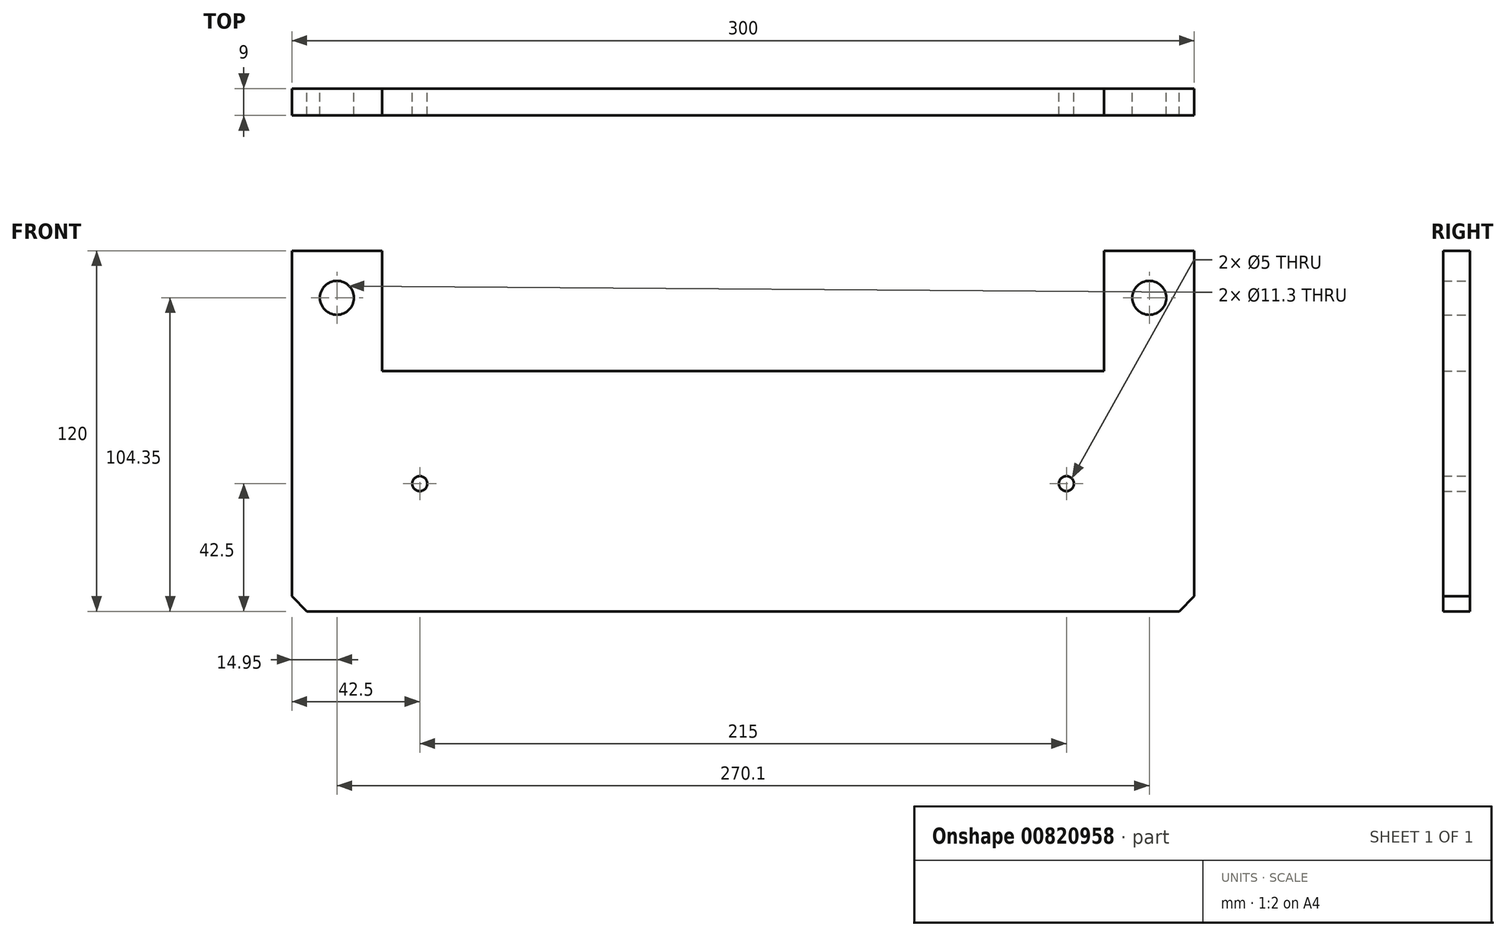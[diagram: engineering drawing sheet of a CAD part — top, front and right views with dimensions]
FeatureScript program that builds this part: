
annotation { "Feature Type Name" : "Feature", "Feature Type Description" : "" }
export const myFeature = defineFeature(function(context is Context, id is Id, definition is map)
    precondition{}
    {
        {
            var Q0;
            Q0=qCreatedBy(makeId("Front.planeOp"),FACE);
            var sketch = newSketch(context, id + "F0", { "sketchPlane" : qUnion([Q0])});
            skCircle(sketch, "E0", {"center": v(-107.5, 42.5) * mm, "radius": 2.5 * mm});
            skLineSegment(sketch, "E1", {"start": v(-150, 120) * mm, "end": v(-120, 120) * mm});
            skLineSegment(sketch, "E2", {"start": v(-120, 120) * mm, "end": v(-120, 80) * mm});
            skLineSegment(sketch, "E3", {"start": v(-120, 80) * mm, "end": v(0, 80) * mm});
            skLineSegment(sketch, "E4", {"start": v(-150, 120) * mm, "end": v(-150, 5) * mm});
            skLineSegment(sketch, "E5", {"start": v(0, 0) * mm, "end": v(-145, 0) * mm});
            skLineSegment(sketch, "E6", {"start": v(-150, 5) * mm, "end": v(-145, 0) * mm});
            skCircle(sketch, "E7", {"center": v(-135.05, 104.35) * mm, "radius": 5.65 * mm});
            skLineSegment(sketch, "E8.MirrorCS", {"start": v(150, 5) * mm, "end": v(145, 0) * mm});
            skCircle(sketch, "E9.MirrorC", {"center": v(107.5, 42.5) * mm, "radius": 2.5 * mm});
            skLineSegment(sketch, "E10.MirrorCS", {"start": v(120, 120) * mm, "end": v(120, 80) * mm});
            skLineSegment(sketch, "E11.MirrorCS", {"start": v(150, 120) * mm, "end": v(120, 120) * mm});
            skLineSegment(sketch, "E12.MirrorCS", {"start": v(150, 120) * mm, "end": v(150, 5) * mm});
            skLineSegment(sketch, "E13.MirrorCS", {"start": v(120, 80) * mm, "end": v(0, 80) * mm});
            skLineSegment(sketch, "E14.MirrorCS", {"start": v(0, 0) * mm, "end": v(145, 0) * mm});
            skCircle(sketch, "E15.MirrorC", {"center": v(135.05, 104.35) * mm, "radius": 5.65 * mm});
            skSolve(sketch);
        }
        {
            var Q0;
            Q0 = qSketchRegion(id + "F0", true);
            extrude(context, id + "F1", {"entities" : qUnion([Q0]), "depth" : 9 * mm, "offsetDistance" : 25 * mm});
        }
    });
